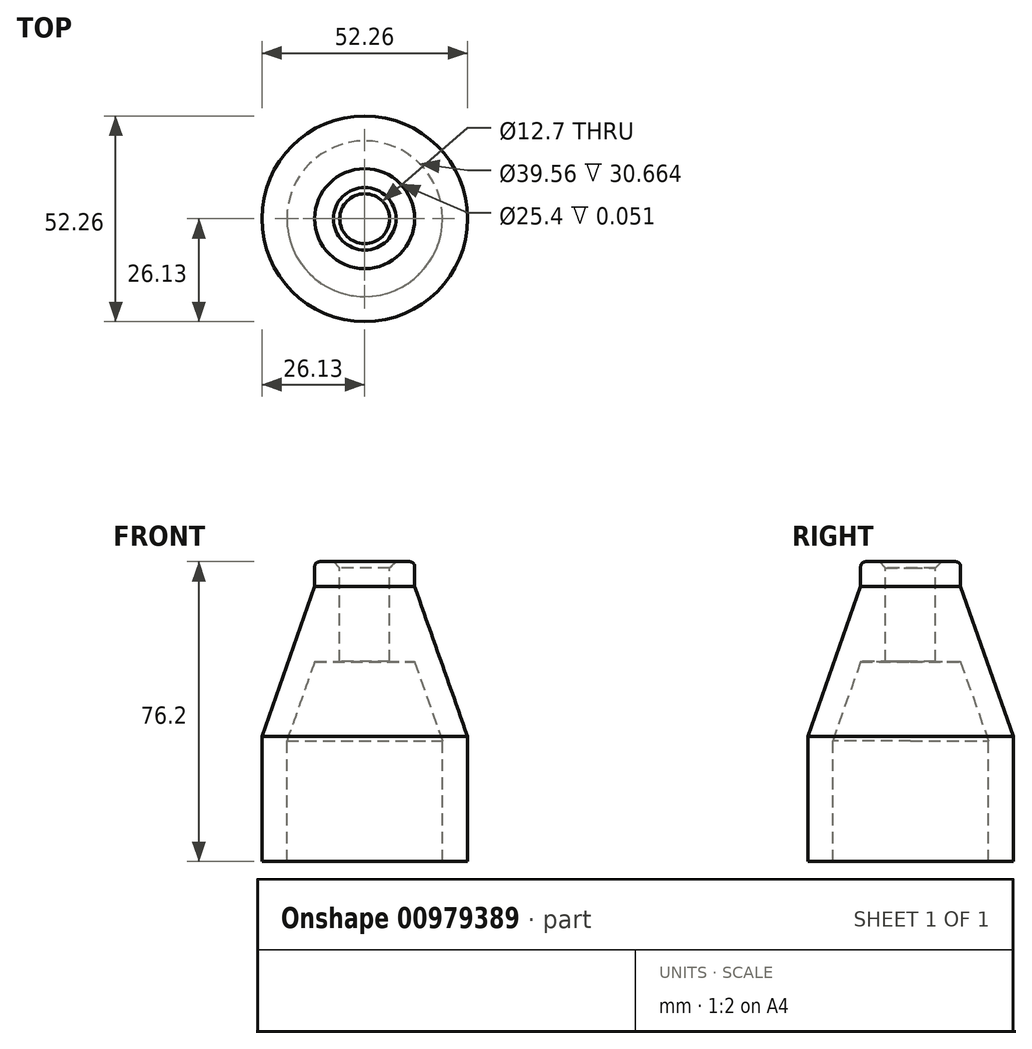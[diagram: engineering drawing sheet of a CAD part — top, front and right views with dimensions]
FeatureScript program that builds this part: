
annotation { "Feature Type Name" : "Feature", "Feature Type Description" : "" }
export const myFeature = defineFeature(function(context is Context, id is Id, definition is map)
    precondition{}
    {
        {
            var Q0;
            Q0=qCreatedBy(makeId("Front.planeOp"),FACE);
            var sketch = newSketch(context, id + "F0", { "sketchPlane" : qUnion([Q0])});
            skLineSegment(sketch, "E0.bottom", {"start": v(0, 0) * mm, "end": v(26.13, 0) * mm});
            skLineSegment(sketch, "E0.left", {"start": v(0, 0) * mm, "end": v(0, 76.2) * mm, "construction": true});
            skLineSegment(sketch, "E0.right", {"start": v(26.13, 0) * mm, "end": v(26.13, 31.75) * mm});
            skLineSegment(sketch, "E1", {"start": v(0, 76.2) * mm, "end": v(12.7, 76.2) * mm});
            skLineSegment(sketch, "E2", {"start": v(12.7, 76.2) * mm, "end": v(12.7, 69.85) * mm});
            skLineSegment(sketch, "E3", {"start": v(12.7, 69.85) * mm, "end": v(26.13, 31.75) * mm});
            skLineSegment(sketch, "E4", {"start": v(0, 76.2) * mm, "end": v(0, 0) * mm});
            skSolve(sketch);
        }
        {
            var Q0;
            Q0=makeQuery(id+"F0.imprint","IMPRINT",FACE,{"disambiguationData":[TD([[makeQuery(id+"F0.imprint","IMPRINT",EDGE,{"derivedFrom":sQuery(id+"F0.wireOp",EDGE,"E0.bottom")}),1.0]])]});
            var Q1;
            Q1=sQuery(id+"F0.wireOp",EDGE,"E4");
            revolve(context, id + "F1", {"surfaceOperationType" : NewSurfaceOperationType.NEW, "entities" : qUnion([Q0]), "axis" : qUnion([Q1]), "revolveType" : RevolveType.FULL});
        }
        {
            var Q0;
            Q0=makeQuery(id+"F1.opRevolve","SWEPT_FACE",FACE,{"disambiguationData":[OSD([sQuery(id+"F0.wireOp",EDGE,"E1")])]});
            var sketch = newSketch(context, id + "F2", { "sketchPlane" : qUnion([Q0])});
            skPoint(sketch, "E5", {"position": v(0, 0) * mm});
            skSolve(sketch);
        }
        {
            var Q0;
            Q0=sQuery(id+"F2.wireOp",VERTEX,"E5");
            var Q1;
            Q1=makeQuery(id+"F1.opRevolve","SWEPT_BODY",BODY,{"disambiguationData":[OSD([sQuery(id+"F0.wireOp",EDGE,"E0.bottom"),sQuery(id+"F0.wireOp",EDGE,"E0.right"),sQuery(id+"F0.wireOp",EDGE,"E1"),sQuery(id+"F0.wireOp",EDGE,"E2"),sQuery(id+"F0.wireOp",EDGE,"E3"),sQuery(id+"F0.wireOp",EDGE,"E4")])]});
            hole(context, id + "F3", {"style" : HoleStyle.C_SINK, "endStyle" : HoleEndStyle.THROUGH, "holeDiameter" : 12.7 * mm, "cSinkDiameter" : 15.88 * mm, "cSinkAngle" : 90 * degree, "majorDiameter" : 6.35 * mm, "isTappedThrough" : true, "tappedDepth" : 12.7 * mm, "tapClearance" : 3, "locations" : qUnion([Q0]), "scope" : qUnion([Q1])});
        }
        {
            var Q0;
            Q0=makeQuery(id+"F1.opRevolve","SWEPT_FACE",FACE,{"disambiguationData":[OSD([sQuery(id+"F0.wireOp",EDGE,"E0.bottom")])]});
            shell(context, id + "F4", {"entities" : qUnion([Q0]), "thickness" : 6.35 * mm});
        }
        {
            var Q0;
            Q0=makeQuery(id+"F4.opShell","OFFSET_FACE",FACE,{"disambiguationData":[OSD([sQuery(id+"F0.wireOp",EDGE,"E0.bottom")])]});
            extrude(context, id + "F5", {"entities" : qUnion([Q0]), "operationType" : NewBodyOperationType.REMOVE, "oppositeDirection" : true, "depth" : 50.8 * mm, "offsetDistance" : 25.4 * mm});
        }
        {
            var Q0;
            Q0=makeQuery(id+"F1.opRevolve","SWEPT_EDGE",EDGE,{"disambiguationData":[OSD([sQuery(id+"F0.wireOp",EDGE,"E1"),sQuery(id+"F0.wireOp",EDGE,"E2")])]});
            fillet(context, id + "F6", {"entities" : qUnion([Q0]), "radius" : ((.25 + .8) + .2) * mm, "tangentPropagation" : true, "allowEdgeOverflow" : false});
        }
    });
